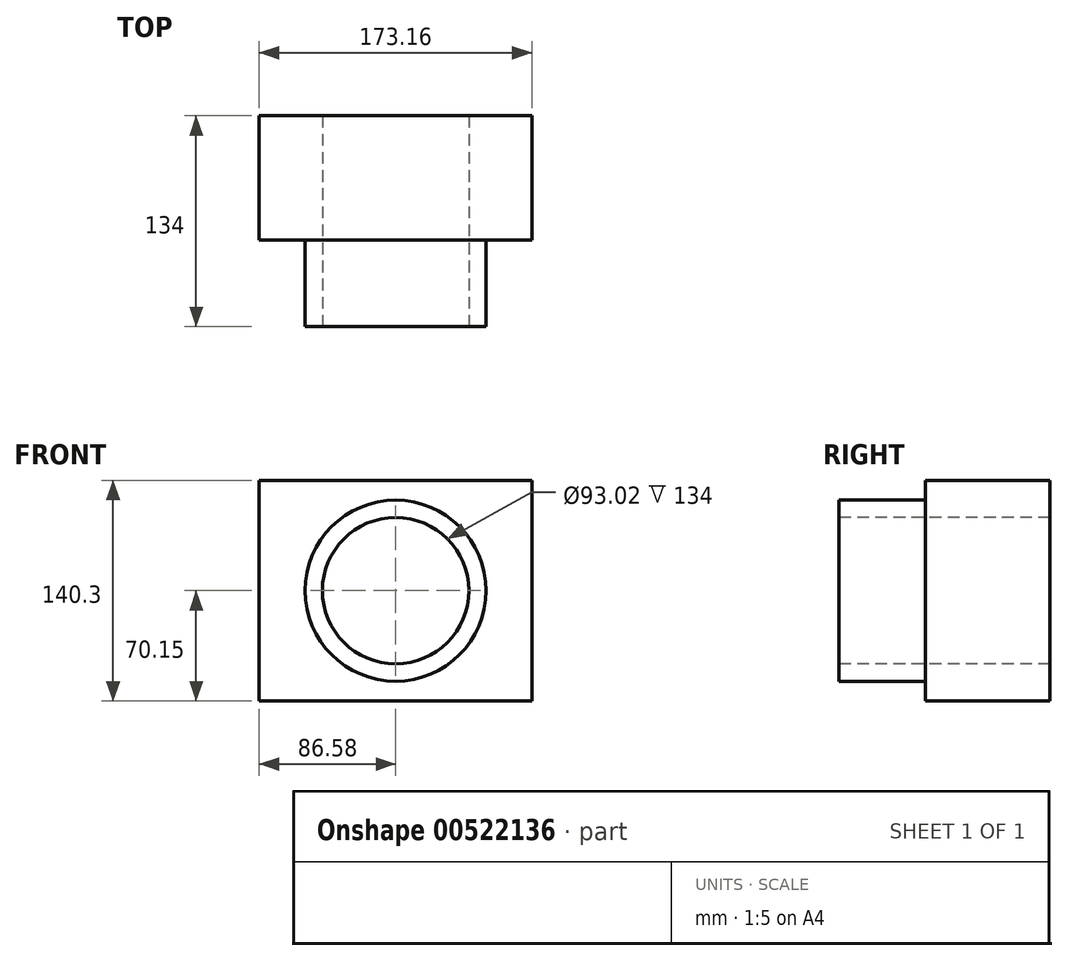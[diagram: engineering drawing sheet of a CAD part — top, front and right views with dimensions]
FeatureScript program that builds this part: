
annotation { "Feature Type Name" : "Feature", "Feature Type Description" : "" }
export const myFeature = defineFeature(function(context is Context, id is Id, definition is map)
    precondition{}
    {
        {
            var Q0;
            Q0=qCreatedBy(makeId("Front.planeOp"),FACE);
            var sketch = newSketch(context, id + "F0", { "sketchPlane" : qUnion([Q0])});
            skLineSegment(sketch, "E0.bottom", {"start": v(86.58, -70.15) * mm, "end": v(-86.58, -70.15) * mm});
            skLineSegment(sketch, "E0.top", {"start": v(86.58, 70.15) * mm, "end": v(-86.58, 70.15) * mm});
            skLineSegment(sketch, "E0.left", {"start": v(86.58, -70.15) * mm, "end": v(86.58, 70.15) * mm});
            skLineSegment(sketch, "E0.right", {"start": v(-86.58, -70.15) * mm, "end": v(-86.58, 70.15) * mm});
            skPoint(sketch, "E0.middle", {"position": v(0, 0) * mm});
            skCircle(sketch, "E1", {"center": v(0, 0) * mm, "radius": 46.51 * mm});
            skSolve(sketch);
        }
        {
            var Q0;
            Q0=makeQuery(id+"F0.imprint","IMPRINT",FACE,{"disambiguationData":[TD([[makeQuery(id+"F0.imprint","IMPRINT",EDGE,{"derivedFrom":sQuery(id+"F0.wireOp",EDGE,"E0.bottom")}),-1.0]])]});
            extrude(context, id + "F1", {"entities" : qUnion([Q0]), "oppositeDirection" : true, "depth" : 79 * mm, "offsetDistance" : 25 * mm});
        }
        {
            var Q0;
            Q0=makeQuery(id+"F1.opExtrude","CAP_FACE",FACE,{"disambiguationData":[OSD([sQuery(id+"F0.wireOp",EDGE,"E0.bottom"),sQuery(id+"F0.wireOp",EDGE,"E0.top"),sQuery(id+"F0.wireOp",EDGE,"E0.left"),sQuery(id+"F0.wireOp",EDGE,"E0.right"),sQuery(id+"F0.wireOp",EDGE,"E1")])],"isStart":true});
            var sketch = newSketch(context, id + "F2", { "sketchPlane" : qUnion([Q0])});
            skCircle(sketch, "E2", {"center": v(0, 0) * mm, "radius": 57.48 * mm});
            skSolve(sketch);
        }
        {
            var Q0;
            Q0=makeQuery(id+"F2.imprint","IMPRINT",FACE,{"disambiguationData":[TD([[makeQuery(id+"F2.imprint","IMPRINT",EDGE,{"derivedFrom":sQuery(id+"F2.wireOp",EDGE,"E2")}),1.0]])]});
            extrude(context, id + "F3", {"entities" : qUnion([Q0]), "operationType" : NewBodyOperationType.ADD, "depth" : 55 * mm, "offsetDistance" : 25 * mm});
        }
    });
